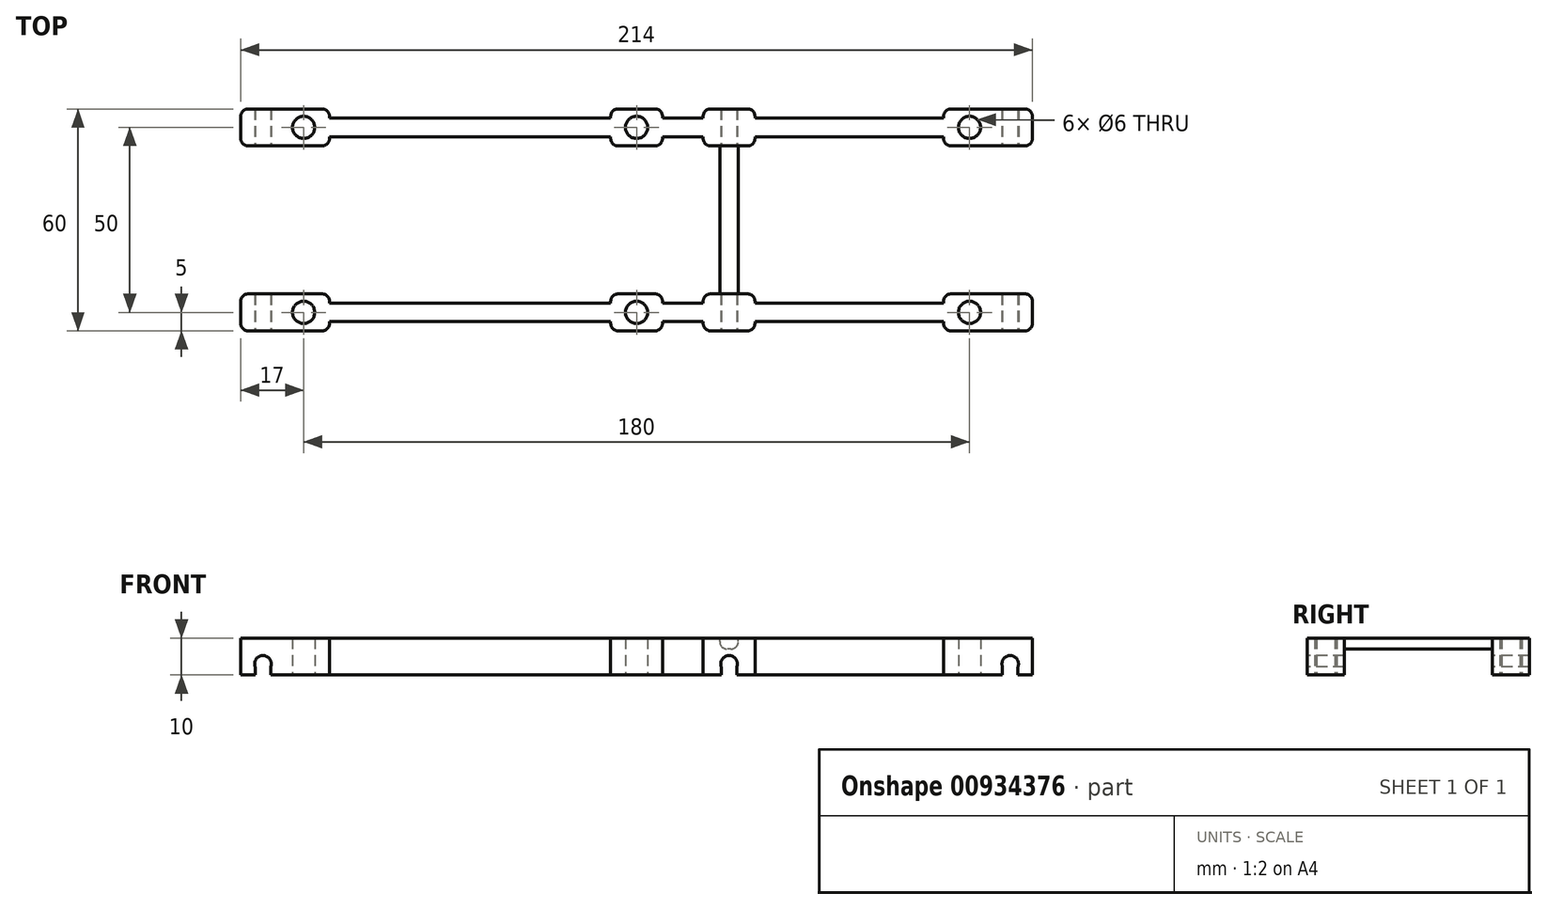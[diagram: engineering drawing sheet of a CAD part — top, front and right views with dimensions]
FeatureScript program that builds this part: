
annotation { "Feature Type Name" : "Feature", "Feature Type Description" : "" }
export const myFeature = defineFeature(function(context is Context, id is Id, definition is map)
    precondition{}
    {
        {
            var Q0;
            Q0=qCreatedBy(makeId("Top.planeOp"),FACE);
            var sketch = newSketch(context, id + "F0", { "sketchPlane" : qUnion([Q0])});
            skPoint(sketch, "E0", {"position": v(0, 25) * mm});
            skPoint(sketch, "E1", {"position": v(0, -25) * mm});
            skLineSegment(sketch, "E2.bottom", {"start": v(107, 20) * mm, "end": v(83, 20) * mm});
            skLineSegment(sketch, "E2.top", {"start": v(107, 30) * mm, "end": v(83, 30) * mm});
            skLineSegment(sketch, "E2.left", {"start": v(107, 20) * mm, "end": v(107, 30) * mm});
            skLineSegment(sketch, "E2.right", {"start": v(-107, 20) * mm, "end": v(-107, 30) * mm});
            skLineSegment(sketch, "E3.bottom", {"start": v(107, -30) * mm, "end": v(83, -30) * mm});
            skLineSegment(sketch, "E3.top", {"start": v(107, -20) * mm, "end": v(83, -20) * mm});
            skLineSegment(sketch, "E3.left", {"start": v(107, -30) * mm, "end": v(107, -20) * mm});
            skLineSegment(sketch, "E3.right", {"start": v(-107, -30) * mm, "end": v(-107, -20) * mm});
            skCircle(sketch, "E4", {"center": v(0, 25) * mm, "radius": 3 * mm});
            skCircle(sketch, "E5", {"center": v(0, -25) * mm, "radius": 3 * mm});
            skPoint(sketch, "E6", {"position": v(-90, 25) * mm});
            skPoint(sketch, "E7", {"position": v(-90, -25) * mm});
            skPoint(sketch, "E8", {"position": v(90, 25) * mm});
            skPoint(sketch, "E9", {"position": v(90, -25) * mm});
            skCircle(sketch, "E10", {"center": v(-90, 25) * mm, "radius": 3 * mm});
            skCircle(sketch, "E11", {"center": v(-90, -25) * mm, "radius": 3 * mm});
            skCircle(sketch, "E12", {"center": v(90, -25) * mm, "radius": 3 * mm});
            skCircle(sketch, "E13", {"center": v(90, 25) * mm, "radius": 3 * mm});
            skPoint(sketch, "E14", {"position": v(-101, 25) * mm});
            skPoint(sketch, "E15", {"position": v(25, 25) * mm});
            skPoint(sketch, "E16", {"position": v(101, 25) * mm});
            skLineSegment(sketch, "E17", {"start": v(-83, 30) * mm, "end": v(-83, 27.5) * mm});
            skLineSegment(sketch, "E18", {"start": v(-83, 27.5) * mm, "end": v(-7, 27.5) * mm});
            skLineSegment(sketch, "E19", {"start": v(-7, 27.5) * mm, "end": v(-7, 27.5) * mm});
            skLineSegment(sketch, "E20", {"start": v(-7, 20) * mm, "end": v(-7, 22.5) * mm});
            skLineSegment(sketch, "E21", {"start": v(-7, 22.5) * mm, "end": v(-83, 22.5) * mm});
            skLineSegment(sketch, "E22", {"start": v(-83, 22.5) * mm, "end": v(-83, 20) * mm});
            skLineSegment(sketch, "E23", {"start": v(7, 30) * mm, "end": v(7, 27.5) * mm});
            skLineSegment(sketch, "E24", {"start": v(7, 27.5) * mm, "end": v(18, 27.5) * mm});
            skLineSegment(sketch, "E25", {"start": v(18, 27.5) * mm, "end": v(18, 30) * mm});
            skLineSegment(sketch, "E26", {"start": v(7, 20) * mm, "end": v(7, 20) * mm});
            skLineSegment(sketch, "E27", {"start": v(7, 22.5) * mm, "end": v(18, 22.5) * mm});
            skLineSegment(sketch, "E28", {"start": v(18, 22.5) * mm, "end": v(18, 20) * mm});
            skLineSegment(sketch, "E29", {"start": v(32, 30) * mm, "end": v(32, 27.5) * mm});
            skLineSegment(sketch, "E30", {"start": v(32, 27.5) * mm, "end": v(83, 27.5) * mm});
            skLineSegment(sketch, "E31", {"start": v(83, 27.5) * mm, "end": v(83, 30) * mm});
            skLineSegment(sketch, "E32", {"start": v(32, 20) * mm, "end": v(32, 20) * mm});
            skLineSegment(sketch, "E33", {"start": v(32, 22.5) * mm, "end": v(83, 22.5) * mm});
            skLineSegment(sketch, "E34", {"start": v(83, 22.5) * mm, "end": v(83, 20) * mm});
            skPoint(sketch, "E35", {"position": v(25, -25) * mm});
            skLineSegment(sketch, "E36", {"start": v(-83, -20) * mm, "end": v(-83, -22.5) * mm});
            skLineSegment(sketch, "E37", {"start": v(-83, -22.5) * mm, "end": v(-7, -22.5) * mm});
            skLineSegment(sketch, "E38", {"start": v(-7, -22.5) * mm, "end": v(-7, -20) * mm});
            skLineSegment(sketch, "E39", {"start": v(7, -20) * mm, "end": v(7, -22.5) * mm});
            skLineSegment(sketch, "E40", {"start": v(7, -22.5) * mm, "end": v(18, -22.5) * mm});
            skLineSegment(sketch, "E41", {"start": v(18, -22.5) * mm, "end": v(18, -20) * mm});
            skLineSegment(sketch, "E42", {"start": v(32, -20) * mm, "end": v(32, -22.5) * mm});
            skLineSegment(sketch, "E43", {"start": v(32, -22.5) * mm, "end": v(83, -22.5) * mm});
            skLineSegment(sketch, "E44", {"start": v(83, -22.5) * mm, "end": v(83, -20) * mm});
            skLineSegment(sketch, "E45", {"start": v(-83, -30) * mm, "end": v(-83, -27.5) * mm});
            skLineSegment(sketch, "E46", {"start": v(-83, -27.5) * mm, "end": v(-7, -27.5) * mm});
            skLineSegment(sketch, "E47", {"start": v(-7, -27.5) * mm, "end": v(-7, -30) * mm});
            skLineSegment(sketch, "E48", {"start": v(7, -30) * mm, "end": v(7, -27.5) * mm});
            skLineSegment(sketch, "E49", {"start": v(7, -27.5) * mm, "end": v(18, -27.5) * mm});
            skLineSegment(sketch, "E50", {"start": v(18, -27.5) * mm, "end": v(18, -30) * mm});
            skLineSegment(sketch, "E51", {"start": v(32, -30) * mm, "end": v(32, -27.5) * mm});
            skLineSegment(sketch, "E52", {"start": v(32, -27.5) * mm, "end": v(83, -27.5) * mm});
            skLineSegment(sketch, "E53", {"start": v(83, -27.5) * mm, "end": v(83, -30) * mm});
            skLineSegment(sketch, "E54", {"start": v(-83, 30) * mm, "end": v(-83, 30) * mm});
            skLineSegment(sketch, "E55", {"start": v(-7, 30) * mm, "end": v(-7, 30) * mm});
            skLineSegment(sketch, "E56", {"start": v(-83, 20) * mm, "end": v(-107, 20) * mm});
            skLineSegment(sketch, "E57", {"start": v(7, 30) * mm, "end": v(-7, 30) * mm});
            skLineSegment(sketch, "E58", {"start": v(32, 30) * mm, "end": v(18, 30) * mm});
            skLineSegment(sketch, "E59", {"start": v(7, 20) * mm, "end": v(7, 22.5) * mm});
            skLineSegment(sketch, "E60", {"start": v(83, 20) * mm, "end": v(83, 20) * mm});
            skLineSegment(sketch, "E61", {"start": v(-83, 30) * mm, "end": v(-107, 30) * mm});
            skLineSegment(sketch, "E62", {"start": v(-7, 27.5) * mm, "end": v(-7, 30) * mm});
            skLineSegment(sketch, "E63", {"start": v(7, 20) * mm, "end": v(-7, 20) * mm});
            skLineSegment(sketch, "E64", {"start": v(18, 20) * mm, "end": v(18, 20) * mm});
            skLineSegment(sketch, "E65", {"start": v(32, 20) * mm, "end": v(18, 20) * mm});
            skLineSegment(sketch, "E66", {"start": v(32, 20) * mm, "end": v(32, 22.5) * mm});
            skLineSegment(sketch, "E67", {"start": v(-83, -20) * mm, "end": v(-107, -20) * mm});
            skLineSegment(sketch, "E68", {"start": v(7, -20) * mm, "end": v(-7, -20) * mm});
            skLineSegment(sketch, "E69", {"start": v(32, -20) * mm, "end": v(18, -20) * mm});
            skLineSegment(sketch, "E70", {"start": v(32, -30) * mm, "end": v(18, -30) * mm});
            skLineSegment(sketch, "E71", {"start": v(7, -30) * mm, "end": v(-7, -30) * mm});
            skLineSegment(sketch, "E72", {"start": v(-83, -30) * mm, "end": v(-107, -30) * mm});
            skLineSegment(sketch, "E73", {"start": v(-7, -30) * mm, "end": v(-7, -30) * mm});
            skSolve(sketch);
        }
        {
            var Q0;
            Q0=makeQuery(id+"F0.imprint","IMPRINT",FACE,{"disambiguationData":[TD([[makeQuery(id+"F0.imprint","IMPRINT",EDGE,{"derivedFrom":sQuery(id+"F0.wireOp",EDGE,"E2.bottom")}),-1.0]])]});
            var Q1;
            Q1=makeQuery(id+"F0.imprint","IMPRINT",FACE,{"disambiguationData":[TD([[makeQuery(id+"F0.imprint","IMPRINT",EDGE,{"derivedFrom":sQuery(id+"F0.wireOp",EDGE,"E3.bottom")}),-1.0]])]});
            extrude(context, id + "F1", {"entities" : qUnion([Q0, Q1]), "depth" : 10 * mm, "offsetDistance" : 25 * mm});
        }
        {
            var Q0;
            Q0=makeQuery(id+"F1.opExtrude","SWEPT_FACE",FACE,{"disambiguationData":[OSD([sQuery(id+"F0.wireOp",EDGE,"E71")])]});
            var sketch = newSketch(context, id + "F2", { "sketchPlane" : qUnion([Q0])});
            skPoint(sketch, "E74", {"position": v(-101, 3) * mm});
            skPoint(sketch, "E75", {"position": v(25, 3) * mm});
            skPoint(sketch, "E76", {"position": v(101, 3) * mm});
            skCircle(sketch, "E77", {"center": v(101, 3) * mm, "radius": 2.25 * mm});
            skLineSegment(sketch, "E78", {"start": v(-101, 3) * mm, "end": v(-101, -2.67) * mm, "construction": true});
            skLineSegment(sketch, "E79", {"start": v(25, 3) * mm, "end": v(25, -4.31) * mm, "construction": true});
            skLineSegment(sketch, "E80", {"start": v(101, 3) * mm, "end": v(101, -1.35) * mm, "construction": true});
            skLineSegment(sketch, "E81.0", {"start": v(-103.1, 5) * mm, "end": v(-103.1, 3.8) * mm});
            skLineSegment(sketch, "E82.0", {"start": v(98.9, 5) * mm, "end": v(98.9, 3.8) * mm});
            skLineSegment(sketch, "E83.0", {"start": v(103.1, 5) * mm, "end": v(103.1, 3.8) * mm});
            skLineSegment(sketch, "E84", {"start": v(-103.1, 2.2) * mm, "end": v(-103.1, 2.2) * mm});
            skLineSegment(sketch, "E85", {"start": v(-103.1, 3.8) * mm, "end": v(-103.1, 3.8) * mm});
            skLineSegment(sketch, "E86", {"start": v(-103.1, 0) * mm, "end": v(-103.1, -2.67) * mm});
            skArc(sketch, "E87", {"start": v(-98.9, 3.8) * mm, "mid": v(-101, 5.25) * mm, "end": v(-103.1, 3.8) * mm});
            skLineSegment(sketch, "E88", {"start": v(-98.9, 2.2) * mm, "end": v(-98.9, 0) * mm});
            skLineSegment(sketch, "E89", {"start": v(-98.9, 0) * mm, "end": v(-98.9, -2.67) * mm});
            skLineSegment(sketch, "E90", {"start": v(-103.1, -2.67) * mm, "end": v(-98.9, -2.67) * mm});
            skLineSegment(sketch, "E91", {"start": v(22.9, -4.31) * mm, "end": v(27.1, -4.31) * mm});
            skLineSegment(sketch, "E92", {"start": v(22.9, 2.2) * mm, "end": v(22.9, -4.31) * mm});
            skArc(sketch, "E93", {"start": v(22.9, 3.8) * mm, "mid": v(25, 0.75) * mm, "end": v(27.1, 3.8) * mm});
            skArc(sketch, "E94", {"start": v(27.1, 3.8) * mm, "mid": v(25, 5.25) * mm, "end": v(22.9, 3.8) * mm});
            skLineSegment(sketch, "E95", {"start": v(27.1, 2.2) * mm, "end": v(27.1, -4.31) * mm});
            skLineSegment(sketch, "E96", {"start": v(98.9, 2.2) * mm, "end": v(98.9, -1.35) * mm});
            skLineSegment(sketch, "E97", {"start": v(103.1, 2.2) * mm, "end": v(103.1, -1.35) * mm});
            skLineSegment(sketch, "E98", {"start": v(98.9, -1.35) * mm, "end": v(103.1, -1.35) * mm});
            skArc(sketch, "E99", {"start": v(-103.1, 2.2) * mm, "mid": v(-100.2, 0.9) * mm, "end": v(-98.9, 3.8) * mm});
            skArc(sketch, "E100", {"start": v(-103.1, 3.8) * mm, "mid": v(-103.25, 3) * mm, "end": v(-103.1, 2.2) * mm});
            skLineSegment(sketch, "E101", {"start": v(-103.1, 2.2) * mm, "end": v(-103.1, 0) * mm});
            skSolve(sketch);
        }
        {
            var Q0;
            {var subQ0=sQuery(id+"F2.wireOp",EDGE,"E87");Q0=makeQuery(id+"F2.imprint","IMPRINT",FACE,{"disambiguationData":[TD([[makeQuery(id+"F2.imprint","IMPRINT",EDGE,{"derivedFrom":subQ0}),1.0]])]});}
            var Q1;
            Q1=makeQuery(id+"F2.imprint","IMPRINT",FACE,{"disambiguationData":[TD([[makeQuery(id+"F2.imprint","IMPRINT",EDGE,{"derivedFrom":sQuery(id+"F2.wireOp",EDGE,"E86")}),1.0]])]});
            var Q2;
            {var subQ2=sQuery(id+"F2.wireOp",EDGE,"E94");Q2=makeQuery(id+"F2.imprint","IMPRINT",FACE,{"disambiguationData":[TD([[makeQuery(id+"F2.imprint","IMPRINT",EDGE,{"derivedFrom":subQ2}),1.0]])]});}
            var Q3;
            Q3=makeQuery(id+"F2.imprint","IMPRINT",FACE,{"disambiguationData":[TD([[makeQuery(id+"F2.imprint","IMPRINT",EDGE,{"derivedFrom":sQuery(id+"F2.wireOp",EDGE,"E91")}),1.0]])]});
            var Q4;
            {var subQ0=sQuery(id+"F2.wireOp",EDGE,"E77");var subQ1=makeQuery(id+"F2.imprint","IMPRINT",VERTEX,{"disambiguationData":[OD(0.0)],"derivedFrom":subQ0});Q4=makeQuery(id+"F2.imprint","IMPRINT",FACE,{"disambiguationData":[TD([[makeQuery(id+"F2.imprint","IMPRINT",EDGE,{"disambiguationData":[TD([[subQ1,1.0]])],"derivedFrom":subQ0}),1.0]])]});}
            var Q5;
            {var subQ0=sQuery(id+"F2.wireOp",EDGE,"E96");Q5=makeQuery(id+"F2.imprint","IMPRINT",FACE,{"disambiguationData":[TD([[makeQuery(id+"F2.imprint","IMPRINT",EDGE,{"derivedFrom":subQ0}),1.0]])]});}
            extrude(context, id + "F3", {"entities" : qUnion([Q0, Q1, Q2, Q3, Q4, Q5]), "operationType" : NewBodyOperationType.REMOVE, "oppositeDirection" : true, "depth" : 70 * mm, "offsetDistance" : 25 * mm});
        }
        {
            var Q0;
            Q0=makeQuery(id+"F1.opExtrude","SWEPT_EDGE",EDGE,{"disambiguationData":[OSD([sQuery(id+"F0.wireOp",EDGE,"E45"),sQuery(id+"F0.wireOp",EDGE,"E72")])]});
            var Q1;
            Q1=makeQuery(id+"F1.opExtrude","SWEPT_EDGE",EDGE,{"disambiguationData":[OSD([sQuery(id+"F0.wireOp",EDGE,"E36"),sQuery(id+"F0.wireOp",EDGE,"E67")])]});
            var Q2;
            Q2=makeQuery(id+"F1.opExtrude","SWEPT_EDGE",EDGE,{"disambiguationData":[OSD([sQuery(id+"F0.wireOp",EDGE,"E3.right"),sQuery(id+"F0.wireOp",EDGE,"E72")])]});
            var Q3;
            Q3=makeQuery(id+"F1.opExtrude","SWEPT_EDGE",EDGE,{"disambiguationData":[OSD([sQuery(id+"F0.wireOp",EDGE,"E3.right"),sQuery(id+"F0.wireOp",EDGE,"E67")])]});
            var Q4;
            Q4=makeQuery(id+"F1.opExtrude","SWEPT_EDGE",EDGE,{"disambiguationData":[OSD([sQuery(id+"F0.wireOp",EDGE,"E2.right"),sQuery(id+"F0.wireOp",EDGE,"E56")])]});
            var Q5;
            Q5=makeQuery(id+"F1.opExtrude","SWEPT_EDGE",EDGE,{"disambiguationData":[OSD([sQuery(id+"F0.wireOp",EDGE,"E2.right"),sQuery(id+"F0.wireOp",EDGE,"E61")])]});
            var Q6;
            Q6=makeQuery(id+"F1.opExtrude","SWEPT_EDGE",EDGE,{"disambiguationData":[OSD([sQuery(id+"F0.wireOp",EDGE,"E38"),sQuery(id+"F0.wireOp",EDGE,"E68")])]});
            var Q7;
            Q7=makeQuery(id+"F1.opExtrude","SWEPT_EDGE",EDGE,{"disambiguationData":[OSD([sQuery(id+"F0.wireOp",EDGE,"E41"),sQuery(id+"F0.wireOp",EDGE,"E69")])]});
            var Q8;
            Q8=makeQuery(id+"F1.opExtrude","SWEPT_EDGE",EDGE,{"disambiguationData":[OSD([sQuery(id+"F0.wireOp",EDGE,"E47"),sQuery(id+"F0.wireOp",EDGE,"E71")])]});
            var Q9;
            Q9=makeQuery(id+"F1.opExtrude","SWEPT_EDGE",EDGE,{"disambiguationData":[OSD([sQuery(id+"F0.wireOp",EDGE,"E50"),sQuery(id+"F0.wireOp",EDGE,"E70")])]});
            var Q10;
            Q10=makeQuery(id+"F1.opExtrude","SWEPT_EDGE",EDGE,{"disambiguationData":[OSD([sQuery(id+"F0.wireOp",EDGE,"E3.top"),sQuery(id+"F0.wireOp",EDGE,"E44")])]});
            var Q11;
            Q11=makeQuery(id+"F1.opExtrude","SWEPT_EDGE",EDGE,{"disambiguationData":[OSD([sQuery(id+"F0.wireOp",EDGE,"E3.bottom"),sQuery(id+"F0.wireOp",EDGE,"E53")])]});
            var Q12;
            Q12=makeQuery(id+"F1.opExtrude","SWEPT_EDGE",EDGE,{"disambiguationData":[OSD([sQuery(id+"F0.wireOp",EDGE,"E20"),sQuery(id+"F0.wireOp",EDGE,"E63")])]});
            var Q13;
            Q13=makeQuery(id+"F1.opExtrude","SWEPT_EDGE",EDGE,{"disambiguationData":[OSD([sQuery(id+"F0.wireOp",EDGE,"E57"),sQuery(id+"F0.wireOp",EDGE,"E62")])]});
            var Q14;
            Q14=makeQuery(id+"F1.opExtrude","SWEPT_EDGE",EDGE,{"disambiguationData":[OSD([sQuery(id+"F0.wireOp",EDGE,"E28"),sQuery(id+"F0.wireOp",EDGE,"E65")])]});
            var Q15;
            Q15=makeQuery(id+"F1.opExtrude","SWEPT_EDGE",EDGE,{"disambiguationData":[OSD([sQuery(id+"F0.wireOp",EDGE,"E25"),sQuery(id+"F0.wireOp",EDGE,"E58")])]});
            var Q16;
            Q16=makeQuery(id+"F1.opExtrude","SWEPT_EDGE",EDGE,{"disambiguationData":[OSD([sQuery(id+"F0.wireOp",EDGE,"E2.bottom"),sQuery(id+"F0.wireOp",EDGE,"E34")])]});
            var Q17;
            Q17=makeQuery(id+"F1.opExtrude","SWEPT_EDGE",EDGE,{"disambiguationData":[OSD([sQuery(id+"F0.wireOp",EDGE,"E2.top"),sQuery(id+"F0.wireOp",EDGE,"E31")])]});
            var Q18;
            Q18=makeQuery(id+"F1.opExtrude","SWEPT_EDGE",EDGE,{"disambiguationData":[OSD([sQuery(id+"F0.wireOp",EDGE,"E22"),sQuery(id+"F0.wireOp",EDGE,"E56")])]});
            var Q19;
            Q19=makeQuery(id+"F1.opExtrude","SWEPT_EDGE",EDGE,{"disambiguationData":[OSD([sQuery(id+"F0.wireOp",EDGE,"E17"),sQuery(id+"F0.wireOp",EDGE,"E61")])]});
            var Q20;
            Q20=makeQuery(id+"F1.opExtrude","SWEPT_EDGE",EDGE,{"disambiguationData":[OSD([sQuery(id+"F0.wireOp",EDGE,"E59"),sQuery(id+"F0.wireOp",EDGE,"E63")])]});
            var Q21;
            Q21=makeQuery(id+"F1.opExtrude","SWEPT_EDGE",EDGE,{"disambiguationData":[OSD([sQuery(id+"F0.wireOp",EDGE,"E23"),sQuery(id+"F0.wireOp",EDGE,"E57")])]});
            var Q22;
            Q22=makeQuery(id+"F1.opExtrude","SWEPT_EDGE",EDGE,{"disambiguationData":[OSD([sQuery(id+"F0.wireOp",EDGE,"E29"),sQuery(id+"F0.wireOp",EDGE,"E58")])]});
            var Q23;
            Q23=makeQuery(id+"F1.opExtrude","SWEPT_EDGE",EDGE,{"disambiguationData":[OSD([sQuery(id+"F0.wireOp",EDGE,"E65"),sQuery(id+"F0.wireOp",EDGE,"E66")])]});
            var Q24;
            Q24=makeQuery(id+"F1.opExtrude","SWEPT_EDGE",EDGE,{"disambiguationData":[OSD([sQuery(id+"F0.wireOp",EDGE,"E2.bottom"),sQuery(id+"F0.wireOp",EDGE,"E2.left")])]});
            var Q25;
            Q25=makeQuery(id+"F1.opExtrude","SWEPT_EDGE",EDGE,{"disambiguationData":[OSD([sQuery(id+"F0.wireOp",EDGE,"E2.top"),sQuery(id+"F0.wireOp",EDGE,"E2.left")])]});
            var Q26;
            Q26=makeQuery(id+"F1.opExtrude","SWEPT_EDGE",EDGE,{"disambiguationData":[OSD([sQuery(id+"F0.wireOp",EDGE,"E3.bottom"),sQuery(id+"F0.wireOp",EDGE,"E3.left")])]});
            var Q27;
            Q27=makeQuery(id+"F1.opExtrude","SWEPT_EDGE",EDGE,{"disambiguationData":[OSD([sQuery(id+"F0.wireOp",EDGE,"E3.top"),sQuery(id+"F0.wireOp",EDGE,"E3.left")])]});
            var Q28;
            Q28=makeQuery(id+"F1.opExtrude","SWEPT_EDGE",EDGE,{"disambiguationData":[OSD([sQuery(id+"F0.wireOp",EDGE,"E42"),sQuery(id+"F0.wireOp",EDGE,"E69")])]});
            var Q29;
            Q29=makeQuery(id+"F1.opExtrude","SWEPT_EDGE",EDGE,{"disambiguationData":[OSD([sQuery(id+"F0.wireOp",EDGE,"E51"),sQuery(id+"F0.wireOp",EDGE,"E70")])]});
            var Q30;
            Q30=makeQuery(id+"F1.opExtrude","SWEPT_EDGE",EDGE,{"disambiguationData":[OSD([sQuery(id+"F0.wireOp",EDGE,"E48"),sQuery(id+"F0.wireOp",EDGE,"E71")])]});
            var Q31;
            Q31=makeQuery(id+"F1.opExtrude","SWEPT_EDGE",EDGE,{"disambiguationData":[OSD([sQuery(id+"F0.wireOp",EDGE,"E39"),sQuery(id+"F0.wireOp",EDGE,"E68")])]});
            fillet(context, id + "F4", {"entities" : qUnion([Q0, Q1, Q2, Q3, Q4, Q5, Q6, Q7, Q8, Q9, Q10, Q11, Q12, Q13, Q14, Q15, Q16, Q17, Q18, Q19, Q20, Q21, Q22, Q23, Q24, Q25, Q26, Q27, Q28, Q29, Q30, Q31]), "radius" : 2 * mm, "tangentPropagation" : true, "allowEdgeOverflow" : false});
        }
        {
            var Q0;
            Q0=makeQuery(id+"F1.opExtrude","CAP_FACE",FACE,{"disambiguationData":[OSD([sQuery(id+"F0.wireOp",EDGE,"E3.bottom"),sQuery(id+"F0.wireOp",EDGE,"E3.top"),sQuery(id+"F0.wireOp",EDGE,"E3.left"),sQuery(id+"F0.wireOp",EDGE,"E3.right"),sQuery(id+"F0.wireOp",EDGE,"E5"),sQuery(id+"F0.wireOp",EDGE,"E11"),sQuery(id+"F0.wireOp",EDGE,"E12"),sQuery(id+"F0.wireOp",EDGE,"E36"),sQuery(id+"F0.wireOp",EDGE,"E37"),sQuery(id+"F0.wireOp",EDGE,"E38"),sQuery(id+"F0.wireOp",EDGE,"E39"),sQuery(id+"F0.wireOp",EDGE,"E40"),sQuery(id+"F0.wireOp",EDGE,"E41"),sQuery(id+"F0.wireOp",EDGE,"E42"),sQuery(id+"F0.wireOp",EDGE,"E43"),sQuery(id+"F0.wireOp",EDGE,"E44"),sQuery(id+"F0.wireOp",EDGE,"E45"),sQuery(id+"F0.wireOp",EDGE,"E46"),sQuery(id+"F0.wireOp",EDGE,"E47"),sQuery(id+"F0.wireOp",EDGE,"E48"),sQuery(id+"F0.wireOp",EDGE,"E49"),sQuery(id+"F0.wireOp",EDGE,"E50"),sQuery(id+"F0.wireOp",EDGE,"E51"),sQuery(id+"F0.wireOp",EDGE,"E52"),sQuery(id+"F0.wireOp",EDGE,"E53"),sQuery(id+"F0.wireOp",EDGE,"E67"),sQuery(id+"F0.wireOp",EDGE,"E68"),sQuery(id+"F0.wireOp",EDGE,"E69"),sQuery(id+"F0.wireOp",EDGE,"E70"),sQuery(id+"F0.wireOp",EDGE,"E71"),sQuery(id+"F0.wireOp",EDGE,"E72")])],"isStart":false});
            var sketch = newSketch(context, id + "F5", { "sketchPlane" : qUnion([Q0])});
            skPoint(sketch, "E102", {"position": v(25, 0) * mm});
            skLineSegment(sketch, "E103.bottom", {"start": v(27.5, -20) * mm, "end": v(22.5, -20) * mm});
            skLineSegment(sketch, "E103.top", {"start": v(27.5, 20) * mm, "end": v(22.5, 20) * mm});
            skLineSegment(sketch, "E103.left", {"start": v(27.5, -20) * mm, "end": v(27.5, 20) * mm});
            skLineSegment(sketch, "E103.right", {"start": v(22.5, -20) * mm, "end": v(22.5, 20) * mm});
            skSolve(sketch);
        }
        {
            var Q0;
            Q0=makeQuery(id+"F5.imprint","IMPRINT",FACE,{"disambiguationData":[TD([[makeQuery(id+"F5.imprint","IMPRINT",EDGE,{"derivedFrom":sQuery(id+"F5.wireOp",EDGE,"E103.bottom")}),-1.0]])]});
            extrude(context, id + "F6", {"entities" : qUnion([Q0]), "oppositeDirection" : true, "depth" : 3 * mm, "offsetDistance" : 25 * mm});
        }
        {
            var Q0;
            Q0=makeQuery(id+"F6.opExtrude","CAP_EDGE",EDGE,{"disambiguationData":[OSD([sQuery(id+"F5.wireOp",EDGE,"E103.left")])],"isStart":false});
            var Q1;
            Q1=makeQuery(id+"F6.opExtrude","CAP_EDGE",EDGE,{"disambiguationData":[OSD([sQuery(id+"F5.wireOp",EDGE,"E103.right")])],"isStart":false});
            fillet(context, id + "F7", {"entities" : qUnion([Q0, Q1]), "radius" : 2 * mm, "tangentPropagation" : true, "allowEdgeOverflow" : false});
        }
    });
